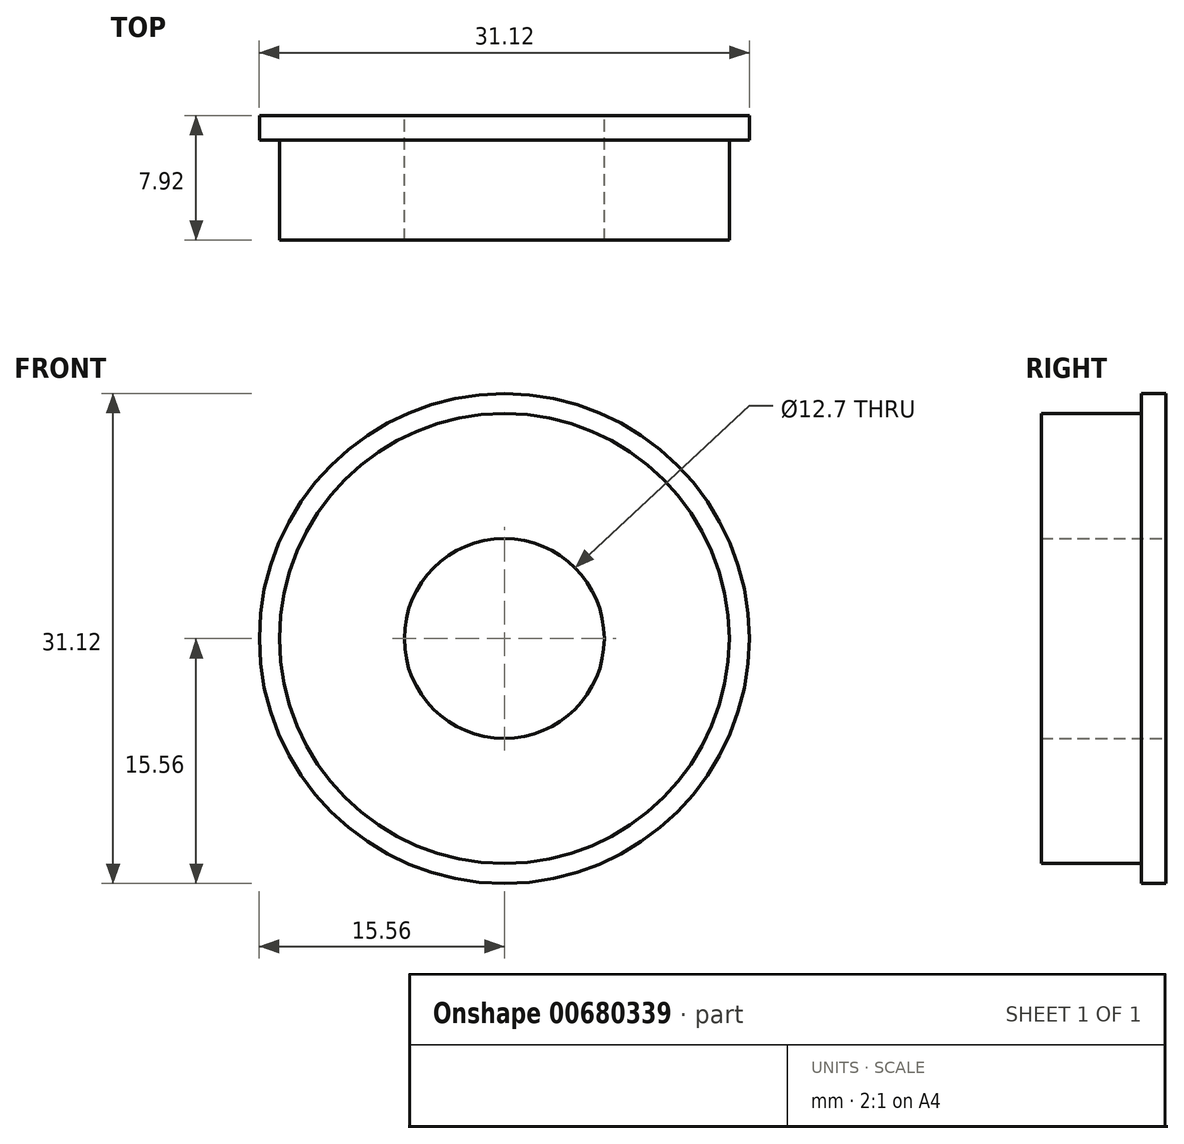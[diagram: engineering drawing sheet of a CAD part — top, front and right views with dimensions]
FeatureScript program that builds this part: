
annotation { "Feature Type Name" : "Feature", "Feature Type Description" : "" }
export const myFeature = defineFeature(function(context is Context, id is Id, definition is map)
    precondition{}
    {
        {
            var Q0;
            Q0=qCreatedBy(makeId("Front.planeOp"),FACE);
            var sketch = newSketch(context, id + "F0", { "sketchPlane" : qUnion([Q0])});
            skCircle(sketch, "E0", {"center": v(0, 0) * mm, "radius": 14.29 * mm});
            skCircle(sketch, "E1", {"center": v(0, 0) * mm, "radius": 6.35 * mm});
            skSolve(sketch);
        }
        {
            var Q0;
            Q0 = qSketchRegion(id + "F0", true);
            extrude(context, id + "F1", {"entities" : qUnion([Q0]), "depth" : 7.92 * mm, "offsetDistance" : 25.4 * mm});
        }
        {
            var Q0;
            Q0=makeQuery(id+"F1.opExtrude","CAP_FACE",FACE,{"disambiguationData":[OSD([sQuery(id+"F0.wireOp",EDGE,"E0"),sQuery(id+"F0.wireOp",EDGE,"E1")])],"isStart":true});
            var sketch = newSketch(context, id + "F2", { "sketchPlane" : qUnion([Q0])});
            skCircle(sketch, "E2", {"center": v(0, 0) * mm, "radius": 15.56 * mm});
            skCircle(sketch, "E3", {"center": v(0, 0) * mm, "radius": 6.35 * mm});
            skSolve(sketch);
        }
        {
            var Q0;
            Q0 = qSketchRegion(id + "F2", true);
            extrude(context, id + "F3", {"entities" : qUnion([Q0]), "operationType" : NewBodyOperationType.ADD, "oppositeDirection" : true, "depth" : 1.57 * mm, "offsetDistance" : 25.4 * mm});
        }
    });
